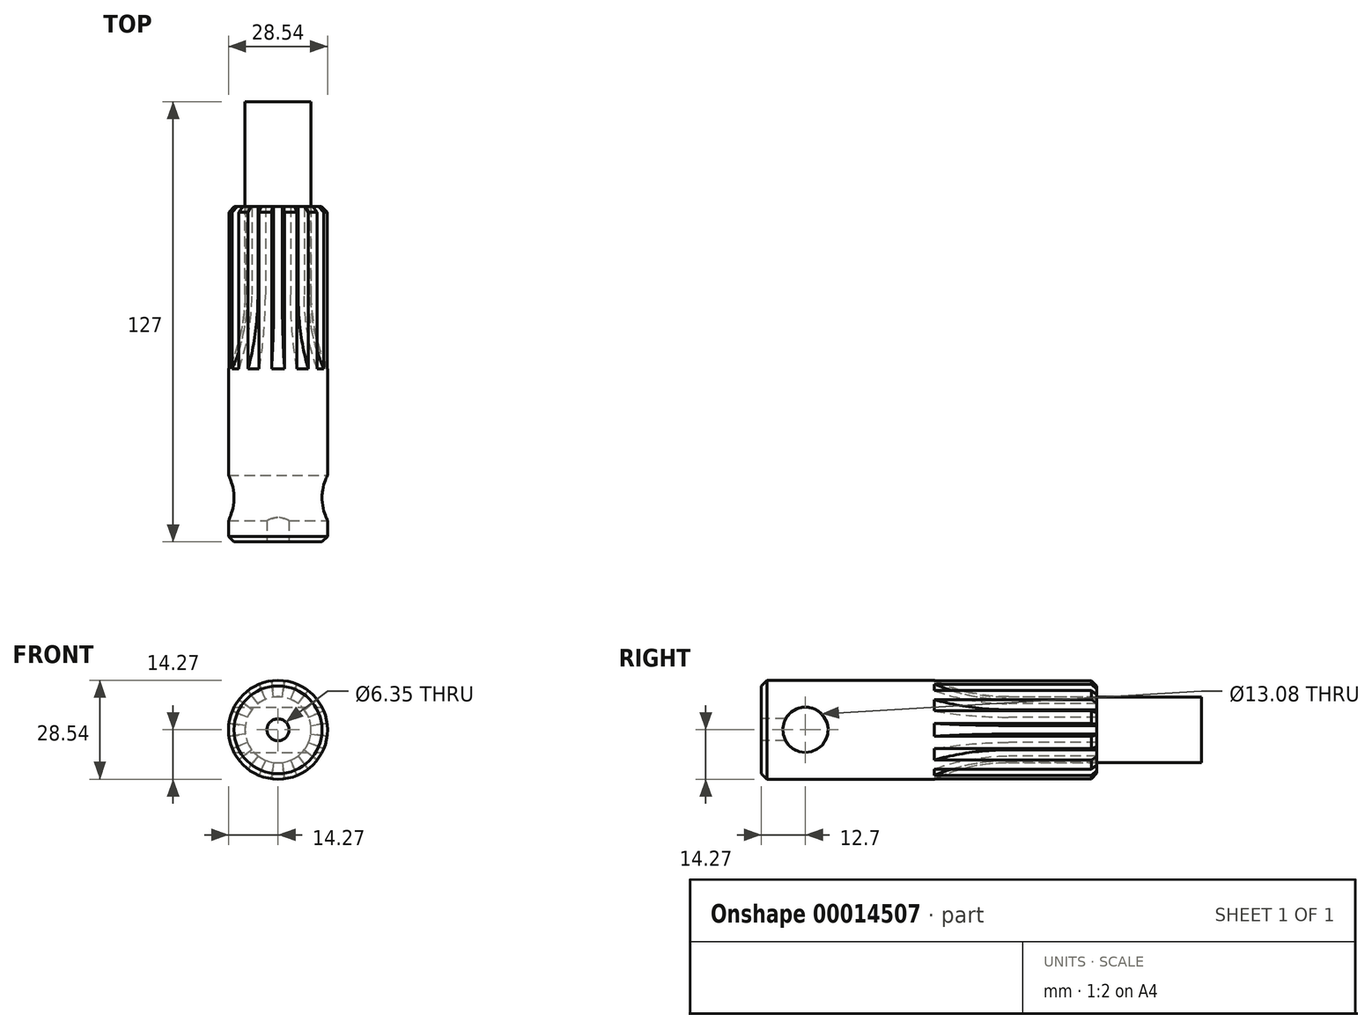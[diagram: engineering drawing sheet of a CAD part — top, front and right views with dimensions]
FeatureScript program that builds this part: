
annotation { "Feature Type Name" : "Feature", "Feature Type Description" : "" }
export const myFeature = defineFeature(function(context is Context, id is Id, definition is map)
    precondition{}
    {
        {
            var Q0;
            Q0=qCreatedBy(makeId("Right.planeOp"),FACE);
            var sketch = newSketch(context, id + "F0", { "sketchPlane" : qUnion([Q0])});
            skLineSegment(sketch, "E0", {"start": v(-154.35, 0) * mm, "end": v(99.65, 0) * mm});
            skSolve(sketch);
        }
        {
            var Q0;
            Q0=qCreatedBy(makeId("Front.planeOp"),FACE);
            var sketch = newSketch(context, id + "F1", { "sketchPlane" : qUnion([Q0])});
            skCircle(sketch, "E1", {"center": v(0, 0) * mm, "radius": 9.51 * mm});
            skSolve(sketch);
        }
        {
            var Q0;
            Q0 = qSketchRegion(id + "F1", true);
            extrude(context, id + "F2", {"entities" : qUnion([Q0]), "depth" : 127 * mm});
        }
        {
            var Q0;
            Q0=makeQuery(id+"F2.opExtrude","CAP_FACE",FACE,{"disambiguationData":[OSD([sQuery(id+"F1.wireOp",EDGE,"E1")])],"isStart":false});
            var sketch = newSketch(context, id + "F3", { "sketchPlane" : qUnion([Q0])});
            skCircle(sketch, "E2", {"center": v(0, 0) * mm, "radius": 14.27 * mm});
            skSolve(sketch);
        }
        {
            var Q0;
            Q0 = qSketchRegion(id + "F3", true);
            extrude(context, id + "F4", {"entities" : qUnion([Q0]), "operationType" : NewBodyOperationType.ADD, "oppositeDirection" : true, "depth" : 96.77 * mm});
        }
        {
            var Q0;
            Q0=qCreatedBy(makeId("Right.planeOp"),FACE);
            var sketch = newSketch(context, id + "F5", { "sketchPlane" : qUnion([Q0])});
            skCircle(sketch, "E3", {"center": v(-114.3, 0) * mm, "radius": 6.54 * mm});
            skSolve(sketch);
        }
        {
            var Q0;
            Q0 = qSketchRegion(id + "F5", true);
            extrude(context, id + "F6", {"entities" : qUnion([Q0]), "operationType" : NewBodyOperationType.REMOVE, "oppositeDirection" : true, "depth" : 50.8 * mm, "symmetric" : true});
        }
        {
            var Q0;
            Q0=makeQuery(id+"F4.boolean.opBoolean","MERGE",FACE,{"derivedFrom":[makeQuery(id+"F2.opExtrude","CAP_FACE",FACE,{"disambiguationData":[OSD([sQuery(id+"F1.wireOp",EDGE,"E1")])],"isStart":false}),makeQuery(id+"F4.opExtrude","CAP_FACE",FACE,{"disambiguationData":[OSD([sQuery(id+"F3.wireOp",EDGE,"E2")])],"isStart":true})]});
            var sketch = newSketch(context, id + "F7", { "sketchPlane" : qUnion([Q0])});
            skCircle(sketch, "E4", {"center": v(0, 0) * mm, "radius": 3.18 * mm});
            skSolve(sketch);
        }
        {
            var Q0;
            Q0 = qSketchRegion(id + "F7", true);
            extrude(context, id + "F8", {"entities" : qUnion([Q0]), "operationType" : NewBodyOperationType.REMOVE, "endBound" : BoundingType.UP_TO_NEXT, "oppositeDirection" : true, "depth" : 25.4 * mm});
        }
        {
            var Q0;
            Q0=qCreatedBy(makeId("Right.planeOp"),FACE);
            var sketch = newSketch(context, id + "F9", { "sketchPlane" : qUnion([Q0])});
            skLineSegment(sketch, "E5", {"start": v(-30.23, 9.52) * mm, "end": v(-55.63, 9.52) * mm});
            skArc(sketch, "E6", {"start": v(-89.23, 22.22) * mm, "mid": v(-73.59, 12.8) * mm, "end": v(-55.63, 9.52) * mm});
            skLineSegment(sketch, "E7", {"start": v(-30.23, 9.52) * mm, "end": v(-30.23, 22.22) * mm});
            skLineSegment(sketch, "E8", {"start": v(-30.23, 22.22) * mm, "end": v(-89.23, 22.22) * mm});
            skSolve(sketch);
        }
        {
            var Q0;
            Q0 = qSketchRegion(id + "F9", true);
            var Q1;
            Q1=sQuery(id+"F0.wireOp",EDGE,"E0");
            revolve(context, id + "F10", {"operationType" : NewBodyOperationType.REMOVE, "entities" : qUnion([Q0]), "axis" : qUnion([Q1]), "revolveType" : RevolveType.SYMMETRIC, "oppositeDirection" : true, "angle" : 15 * degree});
        }
        {
            var Q0;
            Q0=makeQuery(id+"F10.boolean.opBoolean","COPY",FACE,{"derivedFrom":makeQuery(id+"F10.opRevolve","CAP_FACE",FACE,{"disambiguationData":[OSD([sQuery(id+"F9.wireOp",EDGE,"E5"),sQuery(id+"F9.wireOp",EDGE,"E6"),sQuery(id+"F9.wireOp",EDGE,"E7"),sQuery(id+"F9.wireOp",EDGE,"E8")])],"isStart":true})});
            var Q1;
            Q1=makeQuery(id+"F10.boolean.opBoolean","COPY",FACE,{"derivedFrom":makeQuery(id+"F10.opRevolve","SWEPT_FACE",FACE,{"disambiguationData":[OSD([sQuery(id+"F9.wireOp",EDGE,"E5")])]})});
            var Q2;
            Q2=makeQuery(id+"F10.boolean.opBoolean","COPY",FACE,{"derivedFrom":makeQuery(id+"F10.opRevolve","SWEPT_FACE",FACE,{"disambiguationData":[OSD([sQuery(id+"F9.wireOp",EDGE,"E6")])]})});
            var Q3;
            Q3=makeQuery(id+"F10.boolean.opBoolean","COPY",FACE,{"derivedFrom":makeQuery(id+"F10.opRevolve","CAP_FACE",FACE,{"disambiguationData":[OSD([sQuery(id+"F9.wireOp",EDGE,"E5"),sQuery(id+"F9.wireOp",EDGE,"E6"),sQuery(id+"F9.wireOp",EDGE,"E7"),sQuery(id+"F9.wireOp",EDGE,"E8")])],"isStart":false})});
            var Q4;
            Q4=sQuery(id+"F0.wireOp",EDGE,"E0");
            circularPattern(context, id + "F11", {"faces" : qUnion([Q0, Q1, Q2, Q3]), "axis" : qUnion([Q4]), "angle" : 30 * degree, "instanceCount" : 12, "patternType" : PatternType.FACE});
        }
        {
            var Q0;
            Q0=makeQuery(id+"F11.opPattern","SPLIT",EDGE,{"disambiguationData":[OD(0.0)],"derivedFrom":makeQuery(id+"F4.opExtrude","CAP_EDGE",EDGE,{"disambiguationData":[OSD([sQuery(id+"F3.wireOp",EDGE,"E2")])],"isStart":false})});
            var Q1;
            Q1=makeQuery(id+"F11.opPattern","SPLIT",EDGE,{"disambiguationData":[OD(1.0)],"derivedFrom":makeQuery(id+"F4.opExtrude","CAP_EDGE",EDGE,{"disambiguationData":[OSD([sQuery(id+"F3.wireOp",EDGE,"E2")])],"isStart":false})});
            var Q2;
            Q2=makeQuery(id+"F11.opPattern","SPLIT",EDGE,{"disambiguationData":[OD(2.0)],"derivedFrom":makeQuery(id+"F4.opExtrude","CAP_EDGE",EDGE,{"disambiguationData":[OSD([sQuery(id+"F3.wireOp",EDGE,"E2")])],"isStart":false})});
            var Q3;
            Q3=makeQuery(id+"F11.opPattern","SPLIT",EDGE,{"disambiguationData":[OD(3.0)],"derivedFrom":makeQuery(id+"F4.opExtrude","CAP_EDGE",EDGE,{"disambiguationData":[OSD([sQuery(id+"F3.wireOp",EDGE,"E2")])],"isStart":false})});
            var Q4;
            Q4=makeQuery(id+"F11.opPattern","SPLIT",EDGE,{"disambiguationData":[OD(4.0)],"derivedFrom":makeQuery(id+"F4.opExtrude","CAP_EDGE",EDGE,{"disambiguationData":[OSD([sQuery(id+"F3.wireOp",EDGE,"E2")])],"isStart":false})});
            var Q5;
            Q5=makeQuery(id+"F11.opPattern","SPLIT",EDGE,{"disambiguationData":[OD(5.0)],"derivedFrom":makeQuery(id+"F4.opExtrude","CAP_EDGE",EDGE,{"disambiguationData":[OSD([sQuery(id+"F3.wireOp",EDGE,"E2")])],"isStart":false})});
            var Q6;
            Q6=makeQuery(id+"F11.opPattern","SPLIT",EDGE,{"disambiguationData":[OD(6.0)],"derivedFrom":makeQuery(id+"F4.opExtrude","CAP_EDGE",EDGE,{"disambiguationData":[OSD([sQuery(id+"F3.wireOp",EDGE,"E2")])],"isStart":false})});
            var Q7;
            Q7=makeQuery(id+"F11.opPattern","SPLIT",EDGE,{"disambiguationData":[OD(7.0)],"derivedFrom":makeQuery(id+"F4.opExtrude","CAP_EDGE",EDGE,{"disambiguationData":[OSD([sQuery(id+"F3.wireOp",EDGE,"E2")])],"isStart":false})});
            var Q8;
            Q8=makeQuery(id+"F11.opPattern","SPLIT",EDGE,{"disambiguationData":[OD(8.0)],"derivedFrom":makeQuery(id+"F4.opExtrude","CAP_EDGE",EDGE,{"disambiguationData":[OSD([sQuery(id+"F3.wireOp",EDGE,"E2")])],"isStart":false})});
            var Q9;
            Q9=makeQuery(id+"F11.opPattern","SPLIT",EDGE,{"disambiguationData":[OD(9.0)],"derivedFrom":makeQuery(id+"F4.opExtrude","CAP_EDGE",EDGE,{"disambiguationData":[OSD([sQuery(id+"F3.wireOp",EDGE,"E2")])],"isStart":false})});
            var Q10;
            Q10=makeQuery(id+"F11.opPattern","SPLIT",EDGE,{"disambiguationData":[OD(10.0)],"derivedFrom":makeQuery(id+"F4.opExtrude","CAP_EDGE",EDGE,{"disambiguationData":[OSD([sQuery(id+"F3.wireOp",EDGE,"E2")])],"isStart":false})});
            var Q11;
            Q11=makeQuery(id+"F11.opPattern","SPLIT",EDGE,{"disambiguationData":[OD(11.0)],"derivedFrom":makeQuery(id+"F4.opExtrude","CAP_EDGE",EDGE,{"disambiguationData":[OSD([sQuery(id+"F3.wireOp",EDGE,"E2")])],"isStart":false})});
            chamfer(context, id + "F12", {"entities" : qUnion([Q0, Q1, Q2, Q3, Q4, Q5, Q6, Q7, Q8, Q9, Q10, Q11]), "chamferType" : ChamferType.OFFSET_ANGLE, "width" : 1.6 * mm, "oppositeDirection" : false, "angle" : 45 * degree, "tangentPropagation" : true});
        }
        {
            var Q0;
            Q0=makeQuery(id+"F4.opExtrude","CAP_EDGE",EDGE,{"disambiguationData":[OSD([sQuery(id+"F3.wireOp",EDGE,"E2")])],"isStart":true});
            chamfer(context, id + "F13", {"entities" : qUnion([Q0]), "chamferType" : ChamferType.OFFSET_ANGLE, "width" : 1.59 * mm, "oppositeDirection" : false, "angle" : 45 * degree, "tangentPropagation" : true});
        }
    });
